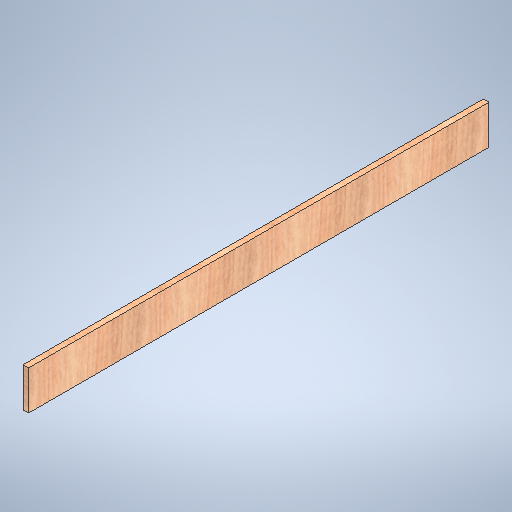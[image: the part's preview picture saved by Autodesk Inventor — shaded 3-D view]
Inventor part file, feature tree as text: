
AUTODESK INVENTOR PART (.ipt)
format: ipt  version: 2025.1 (Build 291241020, 241B)  size: 332,288 bytes
history: native  units: in
note: dims shown in document units (in); Inventor stores cm internally (conversion verified against a paired STEP export)
features: extrude x1, sketch x1
ambient origin geometry x8: Origin, YZ Plane, XZ Plane, XY Plane, X Axis, Y Axis, Z Axis, Center Point
bodies: Solid1 (feature_tree)
feature tree (2):
  extrude  "Extrusion1"  Depth=0.5in TaperAngle=0.0deg
  sketch  "Sketch1"  dims[d1=41.25in d2=0.5in d3=0.0in d4=3.5in]
